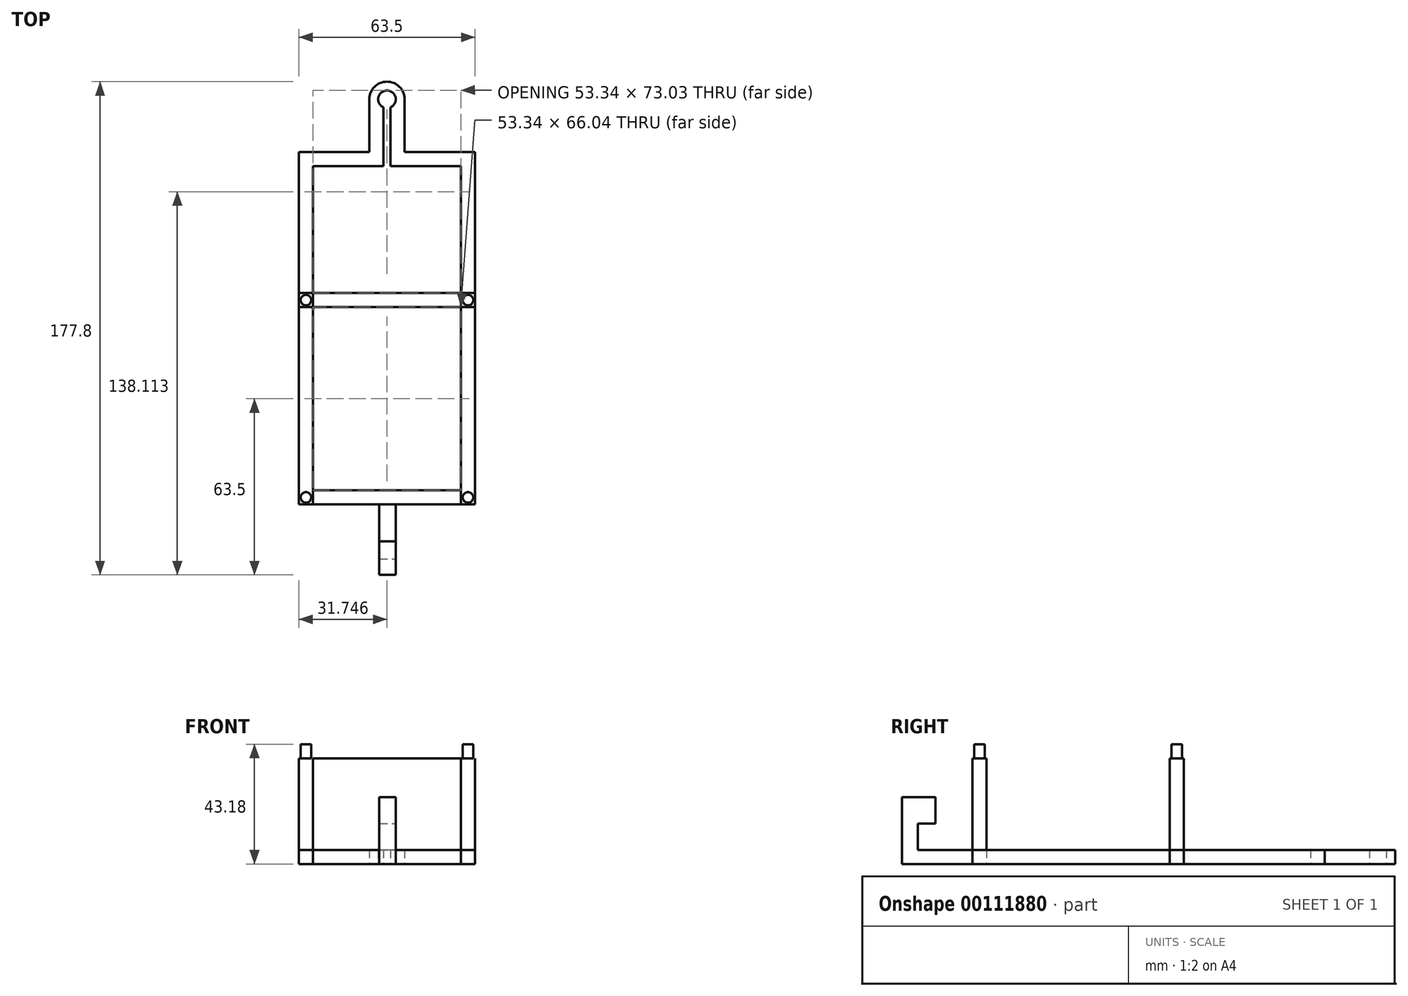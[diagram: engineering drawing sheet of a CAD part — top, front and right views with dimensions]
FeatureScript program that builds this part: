
annotation { "Feature Type Name" : "Feature", "Feature Type Description" : "" }
export const myFeature = defineFeature(function(context is Context, id is Id, definition is map)
    precondition{}
    {
        {
            var Q0;
            Q0=qCreatedBy(makeId("Top.planeOp"),FACE);
            var sketch = newSketch(context, id + "F0", { "sketchPlane" : qUnion([Q0])});
            skCircle(sketch, "E0", {"center": v(-28.44, 19.05) * mm, "radius": 3.17 * mm});
            skCircle(sketch, "E1", {"center": v(-28.44, 19.05) * mm, "radius": 6.35 * mm});
            skLineSegment(sketch, "E2.bottom", {"start": v(-34.8, 19.05) * mm, "end": v(-29.71, 19.05) * mm});
            skLineSegment(sketch, "E2.top", {"start": v(-34.8, 0) * mm, "end": v(-29.71, 0) * mm});
            skLineSegment(sketch, "E2.left", {"start": v(-34.8, 19.05) * mm, "end": v(-34.8, 0) * mm});
            skLineSegment(sketch, "E2.right", {"start": v(-29.71, 19.05) * mm, "end": v(-29.71, 0) * mm});
            skLineSegment(sketch, "E3.bottom", {"start": v(-29.71, 0) * mm, "end": v(-60.2, 0) * mm});
            skLineSegment(sketch, "E3.top", {"start": v(-29.71, -5.08) * mm, "end": v(-60.2, -5.08) * mm});
            skLineSegment(sketch, "E3.left", {"start": v(-29.71, 0) * mm, "end": v(-29.71, -5.08) * mm});
            skLineSegment(sketch, "E3.right", {"start": v(-60.2, 0) * mm, "end": v(-60.2, -5.08) * mm});
            skLineSegment(sketch, "E4.bottom", {"start": v(-60.2, 0) * mm, "end": v(-55.11, 0) * mm});
            skLineSegment(sketch, "E4.top", {"start": v(-60.2, -50.8) * mm, "end": v(-55.11, -50.8) * mm});
            skLineSegment(sketch, "E4.left", {"start": v(-60.2, 0) * mm, "end": v(-60.2, -50.8) * mm});
            skLineSegment(sketch, "E4.right", {"start": v(-55.11, 0) * mm, "end": v(-55.11, -50.8) * mm});
            skLineSegment(sketch, "E5", {"start": v(-28.44, 19.05) * mm, "end": v(-28.44, -72.1) * mm, "construction": true});
            skLineSegment(sketch, "E6.MirrorCS", {"start": v(-22.1, 19.05) * mm, "end": v(-22.1, 0) * mm});
            skLineSegment(sketch, "E7.MirrorCS", {"start": v(-27.17, 19.05) * mm, "end": v(-27.17, 0) * mm});
            skLineSegment(sketch, "E8.MirrorCS", {"start": v(-22.1, 19.05) * mm, "end": v(-27.17, 19.05) * mm});
            skLineSegment(sketch, "E9.MirrorCS", {"start": v(-27.17, 0) * mm, "end": v(3.3, 0) * mm});
            skLineSegment(sketch, "E10.MirrorCS", {"start": v(-27.17, 0) * mm, "end": v(-27.17, -5.08) * mm});
            skLineSegment(sketch, "E11.MirrorCS", {"start": v(-27.17, -5.08) * mm, "end": v(3.3, -5.08) * mm});
            skLineSegment(sketch, "E12.MirrorCS", {"start": v(-1.77, 0) * mm, "end": v(-1.77, -50.8) * mm});
            skLineSegment(sketch, "E13.MirrorCS", {"start": v(3.3, 0) * mm, "end": v(3.3, -50.8) * mm});
            skLineSegment(sketch, "E14.MirrorCS", {"start": v(3.3, -50.8) * mm, "end": v(-1.77, -50.8) * mm});
            skLineSegment(sketch, "E15.bottom", {"start": v(-60.2, -50.8) * mm, "end": v(3.3, -50.8) * mm});
            skLineSegment(sketch, "E15.top", {"start": v(-60.2, -55.88) * mm, "end": v(3.3, -55.88) * mm});
            skLineSegment(sketch, "E15.left", {"start": v(-60.2, -50.8) * mm, "end": v(-60.2, -55.88) * mm});
            skLineSegment(sketch, "E15.right", {"start": v(3.3, -50.8) * mm, "end": v(3.3, -55.88) * mm});
            skLineSegment(sketch, "E16", {"start": v(-55.11, -50.8) * mm, "end": v(-55.11, -55.88) * mm});
            skLineSegment(sketch, "E17", {"start": v(-1.77, -50.8) * mm, "end": v(-1.77, -55.88) * mm});
            skLineSegment(sketch, "E18.bottom", {"start": v(-60.2, -55.88) * mm, "end": v(-55.11, -55.88) * mm});
            skLineSegment(sketch, "E18.top", {"start": v(-60.2, -127) * mm, "end": v(-55.11, -127) * mm});
            skLineSegment(sketch, "E18.left", {"start": v(-60.2, -55.88) * mm, "end": v(-60.2, -127) * mm});
            skLineSegment(sketch, "E18.right", {"start": v(-55.11, -55.88) * mm, "end": v(-55.11, -127) * mm});
            skLineSegment(sketch, "E19.top", {"start": v(3.3, -127) * mm, "end": v(-1.77, -127) * mm});
            skLineSegment(sketch, "E19.left", {"start": v(3.3, -50.8) * mm, "end": v(3.3, -127) * mm});
            skLineSegment(sketch, "E19.right", {"start": v(-1.77, -50.8) * mm, "end": v(-1.77, -127) * mm});
            skLineSegment(sketch, "E20.bottom", {"start": v(-60.2, -127) * mm, "end": v(3.3, -127) * mm});
            skLineSegment(sketch, "E20.top", {"start": v(-60.2, -121.92) * mm, "end": v(3.3, -121.92) * mm});
            skLineSegment(sketch, "E20.left", {"start": v(-60.2, -127) * mm, "end": v(-60.2, -121.92) * mm});
            skLineSegment(sketch, "E20.right", {"start": v(3.3, -127) * mm, "end": v(3.3, -121.92) * mm});
            skSolve(sketch);
        }
        {
            var Q0;
            {var subQ0=sQuery(id+"F0.wireOp",EDGE,"E15.left");Q0=makeQuery(id+"F0.imprint","IMPRINT",FACE,{"disambiguationData":[TD([[makeQuery(id+"F0.imprint","IMPRINT",EDGE,{"derivedFrom":subQ0}),1.0]])]});}
            var Q1;
            {var subQ5=sQuery(id+"F0.wireOp",EDGE,"E14.MirrorCS");Q1=makeQuery(id+"F0.imprint","IMPRINT",FACE,{"disambiguationData":[TD([[makeQuery(id+"F0.imprint","IMPRINT",EDGE,{"derivedFrom":subQ5}),1.0]])]});}
            var Q2;
            {var subQ5=sQuery(id+"F0.wireOp",EDGE,"E20.right");Q2=makeQuery(id+"F0.imprint","IMPRINT",FACE,{"disambiguationData":[TD([[makeQuery(id+"F0.imprint","IMPRINT",EDGE,{"derivedFrom":subQ5}),1.0]])]});}
            var Q3;
            {var subQ5=sQuery(id+"F0.wireOp",EDGE,"E20.left");Q3=makeQuery(id+"F0.imprint","IMPRINT",FACE,{"disambiguationData":[TD([[makeQuery(id+"F0.imprint","IMPRINT",EDGE,{"derivedFrom":subQ5}),-1.0]])]});}
            var Q4;
            {var subQ0=sQuery(id+"F0.wireOp",EDGE,"E20.bottom");var subQ1=sQuery(id+"F0.wireOp",EDGE,"E18.right");var subQ2=makeQuery(id+"F0.imprint","INTERSECT",VERTEX,{"derivedFrom":[subQ1,subQ0]});Q4=makeQuery(id+"F0.imprint","IMPRINT",FACE,{"disambiguationData":[TD([[makeQuery(id+"F0.imprint","IMPRINT",EDGE,{"disambiguationData":[TD([[subQ2,1.0]])],"derivedFrom":subQ1}),1.0]])]});}
            extrude(context, id + "F1", {"entities" : qUnion([Q0, Q1, Q2, Q3, Q4]), "depth" : 38.1 * mm});
        }
        {
            var Q0;
            Q0 = qSketchRegion(id + "F0", true);
            var Q1;
            {var subQ0=sQuery(id+"F0.wireOp",EDGE,"E16");Q1=makeQuery(id+"F0.imprint","IMPRINT",FACE,{"disambiguationData":[TD([[makeQuery(id+"F0.imprint","IMPRINT",EDGE,{"derivedFrom":subQ0}),1.0]])]});}
            extrude(context, id + "F2", {"entities" : qUnion([Q0, Q1]), "depth" : 5.08 * mm});
        }
        {
            var Q0;
            Q0=makeQuery(id+"F1.opExtrude","CAP_FACE",FACE,{"disambiguationData":[OSD([sQuery(id+"F0.wireOp",EDGE,"E15.bottom"),sQuery(id+"F0.wireOp",EDGE,"E15.left"),sQuery(id+"F0.wireOp",EDGE,"E16"),sQuery(id+"F0.wireOp",EDGE,"E18.bottom")])],"isStart":false});
            var sketch = newSketch(context, id + "F3", { "sketchPlane" : qUnion([Q0])});
            skLineSegment(sketch, "E21", {"start": v(-60.2, -50.8) * mm, "end": v(-55.11, -55.88) * mm, "construction": true});
            skLineSegment(sketch, "E22", {"start": v(-55.11, -50.8) * mm, "end": v(-60.2, -55.88) * mm, "construction": true});
            skCircle(sketch, "E23", {"center": v(-57.65, -53.34) * mm, "radius": 1.9 * mm});
            skSolve(sketch);
        }
        {
            var Q0;
            Q0=makeQuery(id+"F1.opExtrude","CAP_FACE",FACE,{"disambiguationData":[OSD([sQuery(id+"F0.wireOp",EDGE,"E15.top"),sQuery(id+"F0.wireOp",EDGE,"E14.MirrorCS"),sQuery(id+"F0.wireOp",EDGE,"E19.left"),sQuery(id+"F0.wireOp",EDGE,"E19.right")])],"isStart":false});
            var sketch = newSketch(context, id + "F4", { "sketchPlane" : qUnion([Q0])});
            skLineSegment(sketch, "E24", {"start": v(-1.77, -50.8) * mm, "end": v(3.3, -55.88) * mm, "construction": true});
            skLineSegment(sketch, "E25", {"start": v(3.3, -50.8) * mm, "end": v(-1.77, -55.88) * mm, "construction": true});
            skCircle(sketch, "E26", {"center": v(0.77, -53.34) * mm, "radius": 1.9 * mm});
            skSolve(sketch);
        }
        {
            var Q0;
            Q0=makeQuery(id+"F1.opExtrude","CAP_FACE",FACE,{"disambiguationData":[OSD([sQuery(id+"F0.wireOp",EDGE,"E20.bottom"),sQuery(id+"F0.wireOp",EDGE,"E20.top"),sQuery(id+"F0.wireOp",EDGE,"E20.left"),sQuery(id+"F0.wireOp",EDGE,"E20.right")])],"isStart":false});
            var sketch = newSketch(context, id + "F5", { "sketchPlane" : qUnion([Q0])});
            skLineSegment(sketch, "E27", {"start": v(-60.2, -121.92) * mm, "end": v(-55.11, -127) * mm, "construction": true});
            skLineSegment(sketch, "E28", {"start": v(-55.11, -121.92) * mm, "end": v(-60.2, -127) * mm, "construction": true});
            skLineSegment(sketch, "E29", {"start": v(3.3, -121.92) * mm, "end": v(-1.77, -127) * mm, "construction": true});
            skLineSegment(sketch, "E30", {"start": v(-1.77, -127) * mm, "end": v(-1.77, -121.92) * mm, "construction": true});
            skLineSegment(sketch, "E31", {"start": v(-1.77, -121.92) * mm, "end": v(3.3, -127) * mm, "construction": true});
            skCircle(sketch, "E32", {"center": v(-57.65, -124.46) * mm, "radius": 1.9 * mm});
            skCircle(sketch, "E33", {"center": v(0.77, -124.46) * mm, "radius": 1.9 * mm});
            skSolve(sketch);
        }
        {
            var Q0;
            Q0 = qSketchRegion(id + "F5", true);
            var Q1;
            Q1 = qSketchRegion(id + "F4", true);
            var Q2;
            Q2 = qSketchRegion(id + "F3", true);
            extrude(context, id + "F6", {"entities" : qUnion([Q0, Q1, Q2]), "operationType" : NewBodyOperationType.ADD, "depth" : 5.08 * mm});
        }
        {
            var Q0;
            Q0=makeQuery(id+"F2.opExtrude","SWEPT_FACE",FACE,{"disambiguationData":[OSD([sQuery(id+"F0.wireOp",EDGE,"E20.bottom")])]});
            var sketch = newSketch(context, id + "F7", { "sketchPlane" : qUnion([Q0])});
            skLineSegment(sketch, "E34.bottom", {"start": v(-31.22, 5.08) * mm, "end": v(-25.24, 5.08) * mm});
            skLineSegment(sketch, "E34.top", {"start": v(-31.22, 0) * mm, "end": v(-25.24, 0) * mm});
            skLineSegment(sketch, "E34.left", {"start": v(-31.22, 5.08) * mm, "end": v(-31.22, 0) * mm});
            skLineSegment(sketch, "E34.right", {"start": v(-25.24, 5.08) * mm, "end": v(-25.24, 0) * mm});
            skSolve(sketch);
        }
        {
            var Q0;
            Q0 = qSketchRegion(id + "F7", true);
            extrude(context, id + "F8", {"entities" : qUnion([Q0]), "depth" : 25.4 * mm});
        }
        {
            var Q0;
            Q0=makeQuery(id+"F8.opExtrude","SWEPT_FACE",FACE,{"disambiguationData":[OSD([sQuery(id+"F7.wireOp",EDGE,"E34.bottom")])]});
            var sketch = newSketch(context, id + "F9", { "sketchPlane" : qUnion([Q0])});
            skLineSegment(sketch, "E35.bottom", {"start": v(-31.22, -146.7) * mm, "end": v(-25.24, -146.7) * mm});
            skLineSegment(sketch, "E35.top", {"start": v(-31.22, -152.4) * mm, "end": v(-25.24, -152.4) * mm});
            skLineSegment(sketch, "E35.left", {"start": v(-31.22, -146.7) * mm, "end": v(-31.22, -152.4) * mm});
            skLineSegment(sketch, "E35.right", {"start": v(-25.24, -146.7) * mm, "end": v(-25.24, -152.4) * mm});
            skSolve(sketch);
        }
        {
            var Q0;
            Q0=makeQuery(id+"F9.imprint","IMPRINT",FACE,{"disambiguationData":[TD([[makeQuery(id+"F9.imprint","IMPRINT",EDGE,{"derivedFrom":sQuery(id+"F9.wireOp",EDGE,"E35.bottom")}),-1.0]])]});
            extrude(context, id + "F10", {"entities" : qUnion([Q0]), "operationType" : NewBodyOperationType.ADD, "depth" : 19.05 * mm});
        }
        {
            var Q0;
            Q0=makeQuery(id+"F10.opExtrude","SWEPT_FACE",FACE,{"disambiguationData":[OSD([sQuery(id+"F9.wireOp",EDGE,"E35.bottom")])]});
            var sketch = newSketch(context, id + "F11", { "sketchPlane" : qUnion([Q0])});
            skLineSegment(sketch, "E36.bottom", {"start": v(31.22, 24.13) * mm, "end": v(25.24, 24.13) * mm});
            skLineSegment(sketch, "E36.top", {"start": v(31.22, 14.6) * mm, "end": v(25.24, 14.6) * mm});
            skLineSegment(sketch, "E36.left", {"start": v(31.22, 24.13) * mm, "end": v(31.22, 14.6) * mm});
            skLineSegment(sketch, "E36.right", {"start": v(25.24, 24.13) * mm, "end": v(25.24, 14.6) * mm});
            skSolve(sketch);
        }
        {
            var Q0;
            Q0=makeQuery(id+"F11.imprint","IMPRINT",FACE,{"disambiguationData":[TD([[makeQuery(id+"F11.imprint","IMPRINT",EDGE,{"derivedFrom":sQuery(id+"F11.wireOp",EDGE,"E36.bottom")}),1.0]])]});
            extrude(context, id + "F12", {"entities" : qUnion([Q0]), "operationType" : NewBodyOperationType.ADD, "depth" : 6.35 * mm});
        }
    });
